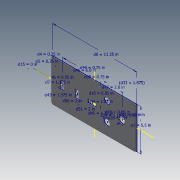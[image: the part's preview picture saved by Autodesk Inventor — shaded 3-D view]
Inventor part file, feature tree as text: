
AUTODESK INVENTOR PART (.ipt)
format: ipt  version: 2020.3 (Build 243373000, 373)  size: 160,256 bytes
history: native  units: in
note: dims shown in document units (in); Inventor stores cm internally (conversion verified against a paired STEP export)
features: hole x2, sketch x1, extrude x1, fillet x1
ambient origin geometry x8: Origin, YZ Plane, XZ Plane, XY Plane, X Axis, Y Axis, Z Axis, Center Point
bodies: Solid1 (feature_tree)
feature tree (5):
  sketch  "Sketch1"  dims[d0=11.25in d1=5.5in d4=0.25in d5=0.25in d6=0.55in d7=1.125in d15=0.0in d16=0.85in d20=0.89in d22=2.3622in d23=0.125in d24=0.0in d25=0.2in d26=0.75in d27=0.375in d28=0.25in d29=0.5635in d30=1.0in d31=0.8108in d32=0.25in d33=1.875in d34=0.58in d35=0.58in d36=0.123in d37=0.75in d38=0.375in d39=0.25in d40=0.5635in d41=1.0in d42=0.8108in d43=1.375in d44=1.25in d45=1.25in d46=6.0in d47=2.0in d48=0.75in d49=0.75in d50=2.0in d51=2.0in]
  extrude  "Extrusion1"  Depth=5.5in
  hole  "Hole1"  [1 undecoded]
  fillet  "Fillet1"  Radius=0.25in
  hole  "Hole2"  [1 undecoded]
note: 2 required parameter values undecoded (feature->parameter linkage not recoverable at this tier; creation-order binding heuristic only, values carry confidence <= 0.55)
